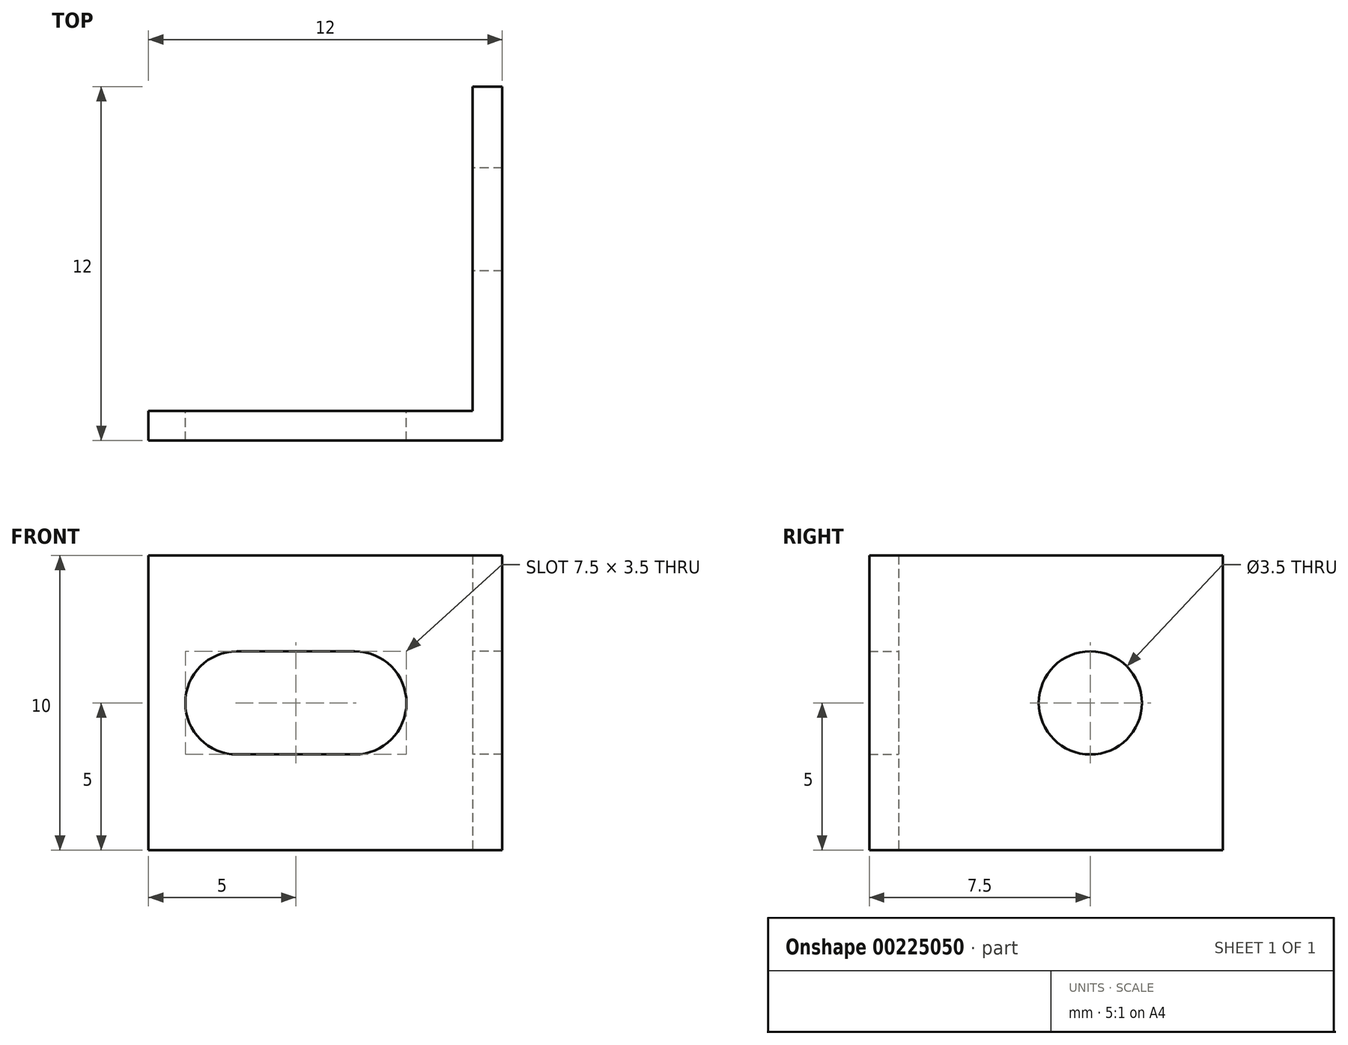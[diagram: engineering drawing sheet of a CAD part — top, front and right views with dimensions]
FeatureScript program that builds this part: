
annotation { "Feature Type Name" : "Feature", "Feature Type Description" : "" }
export const myFeature = defineFeature(function(context is Context, id is Id, definition is map)
    precondition{}
    {
        {
            var Q0;
            Q0=qCreatedBy(makeId("Top.planeOp"),FACE);
            var sketch = newSketch(context, id + "F0", { "sketchPlane" : qUnion([Q0])});
            skLineSegment(sketch, "E0", {"start": v(0, 0) * mm, "end": v(-12, 0) * mm});
            skLineSegment(sketch, "E1", {"start": v(-12, 0) * mm, "end": v(-12, 1) * mm});
            skLineSegment(sketch, "E2", {"start": v(-12, 1) * mm, "end": v(-1, 1) * mm});
            skLineSegment(sketch, "E3", {"start": v(-1, 1) * mm, "end": v(-1, 12) * mm});
            skLineSegment(sketch, "E4", {"start": v(-1, 12) * mm, "end": v(0, 12) * mm});
            skLineSegment(sketch, "E5", {"start": v(0, 12) * mm, "end": v(0, 0) * mm});
            skSolve(sketch);
        }
        {
            var Q0;
            Q0 = qSketchRegion(id + "F0", true);
            extrude(context, id + "F1", {"entities" : qUnion([Q0]), "depth" : 10 * mm});
        }
        {
            var Q0;
            Q0=makeQuery(id+"F1.opExtrude","SWEPT_FACE",FACE,{"disambiguationData":[OSD([sQuery(id+"F0.wireOp",EDGE,"E2")])]});
            var sketch = newSketch(context, id + "F2", { "sketchPlane" : qUnion([Q0])});
            skPoint(sketch, "E6.positionSnap0", {"position": v(12, 5) * mm});
            skArc(sketch, "E7", {"start": v(5, 6.75) * mm, "mid": v(3.25, 5) * mm, "end": v(5, 3.25) * mm});
            skArc(sketch, "E8", {"start": v(9, 3.25) * mm, "mid": v(10.75, 5) * mm, "end": v(9, 6.75) * mm});
            skLineSegment(sketch, "E9", {"start": v(5, 6.75) * mm, "end": v(9, 6.75) * mm});
            skLineSegment(sketch, "E10", {"start": v(9, 3.25) * mm, "end": v(5, 3.25) * mm});
            skSolve(sketch);
        }
        {
            var Q0;
            Q0=makeQuery(id+"F1.opExtrude","SWEPT_FACE",FACE,{"disambiguationData":[OSD([sQuery(id+"F0.wireOp",EDGE,"E3")])]});
            var sketch = newSketch(context, id + "F3", { "sketchPlane" : qUnion([Q0])});
            skPoint(sketch, "E11", {"position": v(-7.5, 5) * mm});
            skPoint(sketch, "E11.positionSnap0", {"position": v(-12, 5) * mm});
            skSolve(sketch);
        }
        {
            var Q0;
            Q0=sQuery(id+"F3.wireOp",VERTEX,"E11");
            var Q1;
            Q1=makeQuery(id+"F1.opExtrude","SWEPT_BODY",BODY,{"disambiguationData":[OSD([sQuery(id+"F0.wireOp",EDGE,"E0"),sQuery(id+"F0.wireOp",EDGE,"E1"),sQuery(id+"F0.wireOp",EDGE,"E2"),sQuery(id+"F0.wireOp",EDGE,"E3"),sQuery(id+"F0.wireOp",EDGE,"E4"),sQuery(id+"F0.wireOp",EDGE,"E5")])]});
            hole(context, id + "F4", {"style" : HoleStyle.SIMPLE, "endStyle" : HoleEndStyle.THROUGH, "holeDiameter" : 3.5 * mm, "locations" : qUnion([Q0]), "scope" : qUnion([Q1]), "isTappedThrough" : true});
        }
        {
            var Q0;
            Q0=makeQuery(id+"F2.imprint","IMPRINT",FACE,{"disambiguationData":[TD([[makeQuery(id+"F2.imprint","IMPRINT",EDGE,{"derivedFrom":sQuery(id+"F2.wireOp",EDGE,"E7")}),1.0]])]});
            extrude(context, id + "F5", {"entities" : qUnion([Q0]), "operationType" : NewBodyOperationType.REMOVE, "oppositeDirection" : true, "depth" : 25 * mm});
        }
    });
